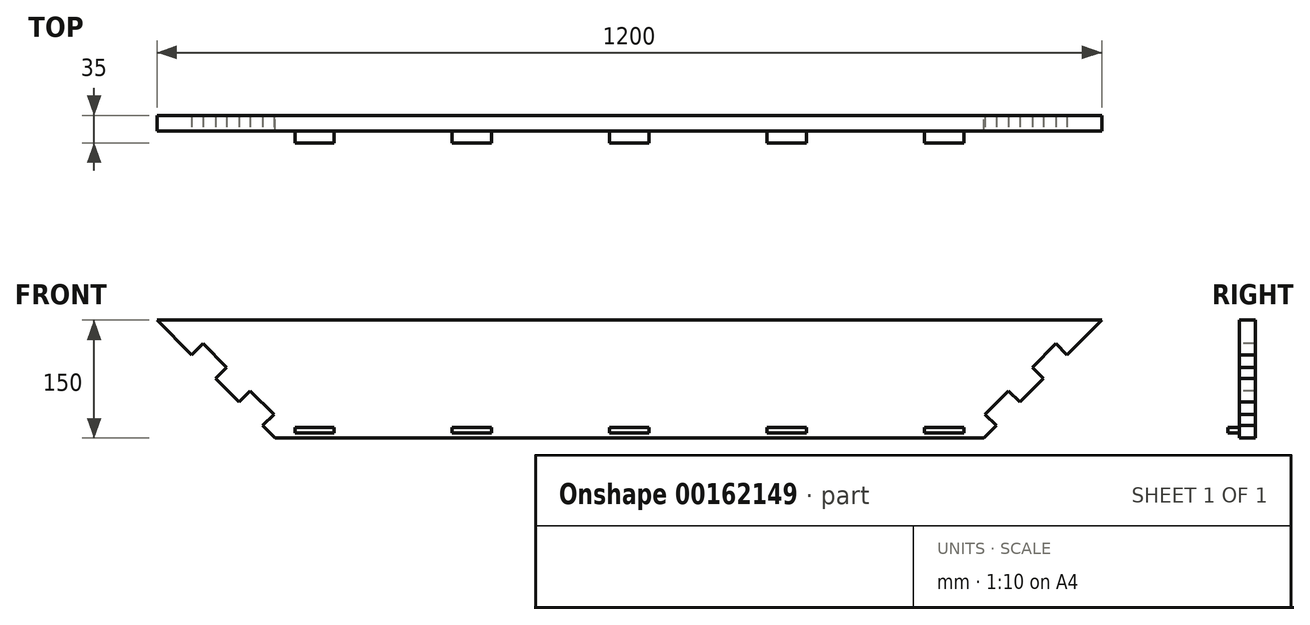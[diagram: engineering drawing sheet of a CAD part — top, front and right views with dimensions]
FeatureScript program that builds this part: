
annotation { "Feature Type Name" : "Feature", "Feature Type Description" : "" }
export const myFeature = defineFeature(function(context is Context, id is Id, definition is map)
    precondition{}
    {
        {
            assignVariable(context, id + "F0", {"name" : "t", "anyValue" : 20 * mm});
        }
        {
            var Q0;
            Q0=qCreatedBy(makeId("Front.planeOp"),FACE);
            var sketch = newSketch(context, id + "F1", { "sketchPlane" : qUnion([Q0])});
            skLineSegment(sketch, "E0.bottom", {"start": v(600, 75) * mm, "end": v(-600, 75) * mm});
            skLineSegment(sketch, "E0.top", {"start": v(600, -75) * mm, "end": v(-600, -75) * mm});
            skLineSegment(sketch, "E0.left", {"start": v(600, 75) * mm, "end": v(600, -75) * mm});
            skLineSegment(sketch, "E0.right", {"start": v(-600, 75) * mm, "end": v(-600, -75) * mm});
            skPoint(sketch, "E0.middle", {"position": v(0, 0) * mm});
            skLineSegment(sketch, "E1", {"start": v(-600, 75) * mm, "end": v(-450, -75) * mm});
            skLineSegment(sketch, "E2.MirrorCS", {"start": v(600, 75) * mm, "end": v(450, -75) * mm});
            skSolve(sketch);
        }
        {
            var Q0;
            {var subQ1=sQuery(id+"F1.wireOp",EDGE,"E0.bottom");Q0=makeQuery(id+"F1.imprint","IMPRINT",FACE,{"disambiguationData":[TD([[makeQuery(id+"F1.imprint","IMPRINT",EDGE,{"derivedFrom":subQ1}),1.0]])]});}
            extrude(context, id + "F2", {"entities" : qUnion([Q0]), "endBound" : BoundingType.SYMMETRIC, "depth" : getVariable(context, 't')});
        }
        {
            var Q0;
            Q0=qCreatedBy(makeId("Front.planeOp"),FACE);
            var sketch = newSketch(context, id + "F3", { "sketchPlane" : qUnion([Q0])});
            skLineSegment(sketch, "E3.bottom", {"start": v(-555.86, 30.86) * mm, "end": v(-541.72, 45) * mm});
            skLineSegment(sketch, "E3.top", {"start": v(-525.86, 0.86) * mm, "end": v(-511.72, 15) * mm});
            skLineSegment(sketch, "E3.left", {"start": v(-555.86, 30.86) * mm, "end": v(-525.86, 0.86) * mm});
            skLineSegment(sketch, "E3.right", {"start": v(-541.72, 45) * mm, "end": v(-511.72, 15) * mm});
            skLineSegment(sketch, "E4", {"start": v(-541.72, 45) * mm, "end": v(-571.72, 75) * mm, "construction": true});
            skLineSegment(sketch, "E5", {"start": v(-511.72, 15) * mm, "end": v(-481.72, -15) * mm, "construction": true});
            skLineSegment(sketch, "E6.bottom", {"start": v(-481.72, -15) * mm, "end": v(-495.86, -29.14) * mm});
            skLineSegment(sketch, "E6.top", {"start": v(-451.72, -45) * mm, "end": v(-465.86, -59.14) * mm});
            skLineSegment(sketch, "E6.left", {"start": v(-481.72, -15) * mm, "end": v(-451.72, -45) * mm});
            skLineSegment(sketch, "E6.right", {"start": v(-495.86, -29.14) * mm, "end": v(-465.86, -59.14) * mm});
            skLineSegment(sketch, "E7.MirrorCS", {"start": v(555.86, 30.86) * mm, "end": v(541.72, 45) * mm});
            skLineSegment(sketch, "E8.MirrorCS", {"start": v(541.72, 45) * mm, "end": v(511.72, 15) * mm});
            skLineSegment(sketch, "E9.MirrorCS", {"start": v(555.86, 30.86) * mm, "end": v(525.86, 0.86) * mm});
            skLineSegment(sketch, "E10.MirrorCS", {"start": v(525.86, 0.86) * mm, "end": v(511.72, 15) * mm});
            skLineSegment(sketch, "E11.MirrorCS", {"start": v(481.72, -15) * mm, "end": v(495.86, -29.14) * mm});
            skLineSegment(sketch, "E12.MirrorCS", {"start": v(481.72, -15) * mm, "end": v(451.72, -45) * mm});
            skLineSegment(sketch, "E13.MirrorCS", {"start": v(451.72, -45) * mm, "end": v(465.86, -59.14) * mm});
            skLineSegment(sketch, "E14.MirrorCS", {"start": v(495.86, -29.14) * mm, "end": v(465.86, -59.14) * mm});
            skLineSegment(sketch, "E15", {"start": v(-451.72, -45) * mm, "end": v(-421.72, -75) * mm, "construction": true});
            skLineSegment(sketch, "E16", {"start": v(-571.72, 75) * mm, "end": v(-585.86, 60.86) * mm, "construction": true});
            skLineSegment(sketch, "E17", {"start": v(-421.72, -75) * mm, "end": v(-435.86, -89.14) * mm, "construction": true});
            skSolve(sketch);
        }
        {
            var Q0;
            Q0 = qSketchRegion(id + "F3", true);
            extrude(context, id + "F4", {"entities" : qUnion([Q0]), "operationType" : NewBodyOperationType.REMOVE, "endBound" : BoundingType.SYMMETRIC, "oppositeDirection" : true, "depth" : getVariable(context, 't')});
        }
        {
            var Q0;
            Q0=makeQuery(id+"F2.opExtrude","CAP_FACE",FACE,{"disambiguationData":[OSD([sQuery(id+"F1.wireOp",EDGE,"E0.bottom"),sQuery(id+"F1.wireOp",EDGE,"E0.top"),sQuery(id+"F1.wireOp",EDGE,"E0.left"),sQuery(id+"F1.wireOp",EDGE,"E0.right"),sQuery(id+"F1.wireOp",EDGE,"E1"),sQuery(id+"F1.wireOp",EDGE,"E2.MirrorCS")])],"isStart":false});
            var sketch = newSketch(context, id + "F5", { "sketchPlane" : qUnion([Q0])});
            skLineSegment(sketch, "E18.bottom", {"start": v(25, -61.67) * mm, "end": v(-25, -61.67) * mm});
            skLineSegment(sketch, "E18.top", {"start": v(25, -68.33) * mm, "end": v(-25, -68.33) * mm});
            skLineSegment(sketch, "E18.left", {"start": v(25, -61.67) * mm, "end": v(25, -68.33) * mm});
            skLineSegment(sketch, "E18.right", {"start": v(-25, -61.67) * mm, "end": v(-25, -68.33) * mm});
            skPoint(sketch, "E18.middle", {"position": v(0, -65) * mm});
            skLineSegment(sketch, "E19.1.0.0", {"start": v(225, -61.67) * mm, "end": v(175, -61.67) * mm});
            skLineSegment(sketch, "E19.1.0.1", {"start": v(225, -61.67) * mm, "end": v(225, -68.33) * mm});
            skLineSegment(sketch, "E19.1.0.2", {"start": v(225, -68.33) * mm, "end": v(175, -68.33) * mm});
            skLineSegment(sketch, "E19.1.0.3", {"start": v(175, -61.67) * mm, "end": v(175, -68.33) * mm});
            skLineSegment(sketch, "E19.2.0.0", {"start": v(425, -61.67) * mm, "end": v(375, -61.67) * mm});
            skLineSegment(sketch, "E19.2.0.1", {"start": v(425, -61.67) * mm, "end": v(425, -68.33) * mm});
            skLineSegment(sketch, "E19.2.0.2", {"start": v(425, -68.33) * mm, "end": v(375, -68.33) * mm});
            skLineSegment(sketch, "E19.2.0.3", {"start": v(375, -61.67) * mm, "end": v(375, -68.33) * mm});
            skLineSegment(sketch, "E19.direction1", {"start": v(-25, -61.67) * mm, "end": v(175, -61.67) * mm, "construction": true});
            skLineSegment(sketch, "E20.MirrorCS", {"start": v(-175, -61.67) * mm, "end": v(-175, -68.33) * mm});
            skLineSegment(sketch, "E21.MirrorCS", {"start": v(-225, -61.67) * mm, "end": v(-175, -61.67) * mm});
            skLineSegment(sketch, "E22.MirrorCS", {"start": v(-225, -68.33) * mm, "end": v(-175, -68.33) * mm});
            skLineSegment(sketch, "E23.MirrorCS", {"start": v(-225, -61.67) * mm, "end": v(-225, -68.33) * mm});
            skLineSegment(sketch, "E24.MirrorCS", {"start": v(-425, -61.67) * mm, "end": v(-425, -68.33) * mm});
            skLineSegment(sketch, "E25.MirrorCS", {"start": v(-375, -61.67) * mm, "end": v(-375, -68.33) * mm});
            skLineSegment(sketch, "E26.MirrorCS", {"start": v(-425, -61.67) * mm, "end": v(-375, -61.67) * mm});
            skLineSegment(sketch, "E27.MirrorCS", {"start": v(-425, -68.33) * mm, "end": v(-375, -68.33) * mm});
            skLineSegment(sketch, "E28", {"start": v(0, -68.33) * mm, "end": v(0, -75) * mm, "construction": true});
            skSolve(sketch);
        }
        {
            var Q0;
            Q0 = qSketchRegion(id + "F5", true);
            extrude(context, id + "F6", {"entities" : qUnion([Q0]), "operationType" : NewBodyOperationType.ADD, "depth" : getVariable(context, 't') / 2 + 5 * mm});
        }
    });
